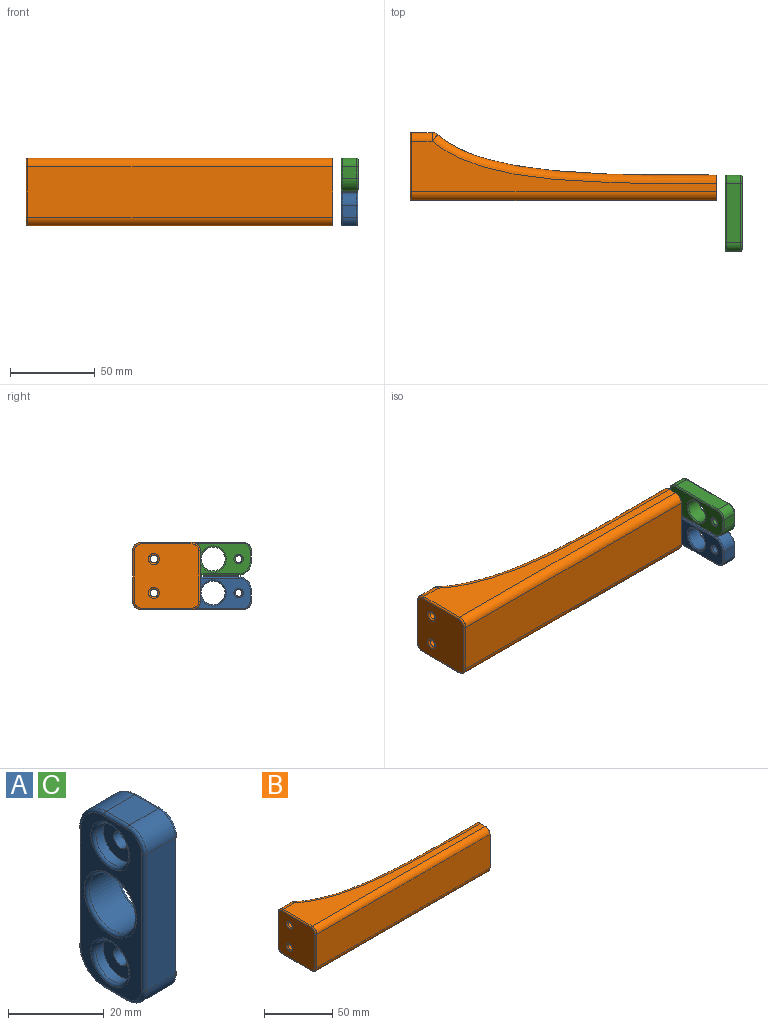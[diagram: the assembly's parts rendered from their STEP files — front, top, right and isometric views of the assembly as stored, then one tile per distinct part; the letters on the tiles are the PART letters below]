
ASSEMBLY  parts=3 mates=2
PART A: 39 faces, bbox 10x20.5x46.2 mm
  f0: plane 30x8.5mm, normal (0,1,0), area 255mm2, adj f14,f15,f21,f30
  f1: plane 8.5x7mm, normal (0,0,1), area 59.5mm2, adj f12,f14,f22,f29
  f2: plane 35x8.5mm, normal (0,-1,0), area 297.5mm2, adj f12,f13,f18,f25
  f3: plane 8.5x7mm, normal (0,0,-1), area 59.5mm2, adj f13,f15,f17,f26
  f4: plane 43.5x18mm, normal (1,0,0), area 519.5mm2, adj f16,f17,f18,f19,f20,f21,f22,f23
  f5: plane 43.5x18mm, normal (-1,0,0), area 359.3mm2, adj f24,f25,f26,f27,f28,f29,f30,f31
  f6: cylinder r=2mm len=6.25mm, axis (-1,0,0), area 78.5mm2, adj f7,f34
  f7: plane 10x10mm, normal (-1,0,0), area 66mm2, adj f6,f8
  f8: cylinder r=5mm len=10mm, axis (-1,0,0), area 70.7mm2, adj f7,f35
  f9: cylinder r=2mm len=6.25mm, axis (-1,0,0), area 78.5mm2, adj f10,f32
  f10: plane 10x10mm, normal (-1,0,0), area 66mm2, adj f9,f11
  f11: cylinder r=5mm len=10mm, axis (-1,0,0), area 70.7mm2, adj f10,f33
  f12: cylinder r=5mm len=8.5mm, axis (-1,0,0), area 66.8mm2, adj f1,f2,f20,f27
  f13: cylinder r=5mm len=8.5mm, axis (-1,0,0), area 66.8mm2, adj f2,f3,f16,f24
  f14: cylinder r=7.5mm len=8.5mm, axis (-1,0,0), area 100.1mm2, adj f0,f1,f23,f31
  f15: cylinder r=7.5mm len=8.5mm, axis (-1,0,0), area 100.1mm2, adj f0,f3,f19,f28
  f16: torus R=4.25mm, axis (1,0,0), area 8.7mm2, adj f4,f13,f17,f18
  f17: cylinder r=0.75mm len=7mm, axis (0,-1,0), area 8.2mm2, adj f3,f4,f16,f19
  f18: cylinder r=0.75mm len=35mm, axis (0,0,1), area 41.2mm2, adj f2,f4,f16,f20
  f19: torus R=6.75mm, axis (1,0,0), area 13.4mm2, adj f4,f15,f17,f21
  f20: torus R=4.25mm, axis (1,0,0), area 8.7mm2, adj f4,f12,f18,f22
  f21: cylinder r=0.75mm len=30mm, axis (0,0,-1), area 35.3mm2, adj f0,f4,f19,f23
  f22: cylinder r=0.75mm len=7mm, axis (0,1,0), area 8.2mm2, adj f1,f4,f20,f23
  f23: torus R=6.75mm, axis (1,0,0), area 13.4mm2, adj f4,f14,f21,f22
  f24: torus R=4.25mm, axis (1,0,0), area 8.7mm2, adj f5,f13,f25,f26
  f25: cylinder r=0.75mm len=35mm, axis (0,0,-1), area 41.2mm2, adj f2,f5,f24,f27
  f26: cylinder r=0.75mm len=7mm, axis (0,1,0), area 8.2mm2, adj f3,f5,f24,f28
  f27: torus R=4.25mm, axis (1,0,0), area 8.7mm2, adj f5,f12,f25,f29
  f28: torus R=6.75mm, axis (1,0,0), area 13.4mm2, adj f5,f15,f26,f30
  f29: cylinder r=0.75mm len=7mm, axis (0,-1,0), area 8.2mm2, adj f1,f5,f27,f31
  f30: cylinder r=0.75mm len=30mm, axis (0,0,1), area 35.3mm2, adj f0,f5,f28,f31
  f31: torus R=6.75mm, axis (1,0,0), area 13.4mm2, adj f5,f14,f29,f30
  f32: torus R=2.75mm, axis (1,0,0), area 16.8mm2, adj f4,f9
  f33: torus R=5.75mm, axis (1,0,0), area 39mm2, adj f5,f11
  f34: torus R=2.75mm, axis (1,0,0), area 16.8mm2, adj f4,f6
  f35: torus R=5.75mm, axis (1,0,0), area 39mm2, adj f5,f8
  f36: cylinder r=7mm len=14mm, axis (-1,0,0), area 373.8mm2, adj f37,f38
  f37: torus R=7.75mm, axis (1,0,0), area 53.8mm2, adj f4,f36
  f38: torus R=7.75mm, axis (1,0,0), area 53.8mm2, adj f5,f36
PART B: 38 faces, bbox 187.5x41x41 mm
  f0: extruded ~164.63x30mm, area 4296.8mm2, adj f3,f17,f18,f19,f22,f25
  f1: plane 38x38mm, normal (-1,0,0), area 1363.9mm2, adj f28,f29,f30,f31,f32,f33,f34,f35
  f2: plane 179.98x30mm, normal (0,-1,0), area 5399.3mm2, adj f3,f26,f27,f34
  f3: plane 40.17x15.17mm, normal (1,0,0), area 558.5mm2, adj f0,f2,f5,f6,f14,f16,f19,f22
  f4: plane 30x12.04mm, normal (0,1,0), area 361.2mm2, adj f20,f21,f25,f29
  f5: plane 179.99x30.01mm, normal (0,0,1), area 1956.9mm2, adj f3,f19,f20,f27,f30
  f6: plane 179.98x30.01mm, normal (0,0,-1), area 1956.9mm2, adj f3,f21,f22,f26,f33
  f7: cylinder r=2.25mm len=4.5mm, axis (1,0,0), area 56.5mm2, adj f8,f37
  f8: plane 10x10mm, normal (1,0,0), area 62.6mm2, adj f7,f9
  f9: cylinder r=5mm len=47.06mm, axis (1,0,0), area 849.7mm2, adj f8,f18
  f10: cylinder r=2.25mm len=4.5mm, axis (1,0,0), area 56.5mm2, adj f11,f36
  f11: plane 10x10mm, normal (1,0,0), area 62.6mm2, adj f10,f12
  f12: cylinder r=5mm len=47.06mm, axis (1,0,0), area 849.7mm2, adj f11,f17
  f13: cone r=0mm half-angle=59deg, axis (1,0,0), area 11.7mm2, adj f14
  f14: cylinder r=1.79mm len=15mm, axis (1,0,0), area 168.3mm2, adj f3,f13
  f15: cone r=0mm half-angle=59deg, axis (1,0,0), area 11.7mm2, adj f16
  f16: cylinder r=1.79mm len=15mm, axis (1,0,0), area 168.3mm2, adj f3,f15
  f17: bspline ~35.6x14.99mm, area 253.5mm2, adj f0,f12,f22
  f18: bspline ~35.67x15.01mm, area 248.9mm2, adj f0,f9,f19
  f19: bspline ~175.04x29.4mm, area 1337.3mm2, adj f0,f3,f5,f18,f23
  f20: cylinder r=5mm len=12.04mm, axis (1,0,0), area 94.6mm2, adj f4,f5,f23,f28
  f21: cylinder r=5mm len=12.04mm, axis (-1,0,0), area 94.6mm2, adj f4,f6,f24,f31
  f22: bspline ~175.04x29.4mm, area 1317.6mm2, adj f0,f3,f6,f17,f24
  f23: sphere r=5mm, area 25.8mm2, adj f19,f20,f25
  f24: sphere r=5mm, area 18.1mm2, adj f21,f22,f25
  f25: cylinder r=5mm len=30mm, axis (0,0,-1), area 108.3mm2, adj f0,f4,f23,f24
  f26: cylinder r=5mm len=179.98mm, axis (1,0,0), area 1413.5mm2, adj f2,f3,f6,f35
  f27: cylinder r=5mm len=179.98mm, axis (-1,0,0), area 1413.5mm2, adj f2,f3,f5,f32
  f28: torus R=4mm, axis (-1,0,0), area 11.4mm2, adj f1,f20,f29,f30
  f29: cylinder r=1mm len=30mm, axis (0,0,-1), area 47.1mm2, adj f1,f4,f28,f31
  f30: cylinder r=1mm len=30mm, axis (0,1,0), area 47.1mm2, adj f1,f5,f28,f32
  f31: torus R=4mm, axis (-1,0,0), area 11.4mm2, adj f1,f21,f29,f33
  f32: torus R=4mm, axis (-1,0,0), area 11.4mm2, adj f1,f27,f30,f34
  f33: cylinder r=1mm len=30mm, axis (0,-1,0), area 47.1mm2, adj f1,f6,f31,f35
  f34: cylinder r=1mm len=30mm, axis (0,0,1), area 47.1mm2, adj f1,f2,f32,f35
  f35: torus R=4mm, axis (-1,0,0), area 11.4mm2, adj f1,f26,f33,f34
  f36: torus R=3.25mm, axis (-1,0,0), area 25.8mm2, adj f1,f10
  f37: torus R=3.25mm, axis (-1,0,0), area 25.8mm2, adj f1,f7
PART C: same geometry as A
PLACE A rot(axis=(0,0.71,0.71),180deg) t=(195.4,12.62,1.93)mm
PLACE B rot(axis=(1,0,0),0deg) t=(-0.57,35.12,-8.07)mm
PLACE C rot(axis=(0,-0.71,0.71),180deg) t=(195.4,42.62,21.93)mm
MATE cylindrical C.f6 <-> B.f15  axis (-1,0,0) through (185.4,42.62,21.93)mm
MATE cylindrical A.f9 <-> B.f13  axis (-1,0,0) through (185.4,42.62,1.93)mm
